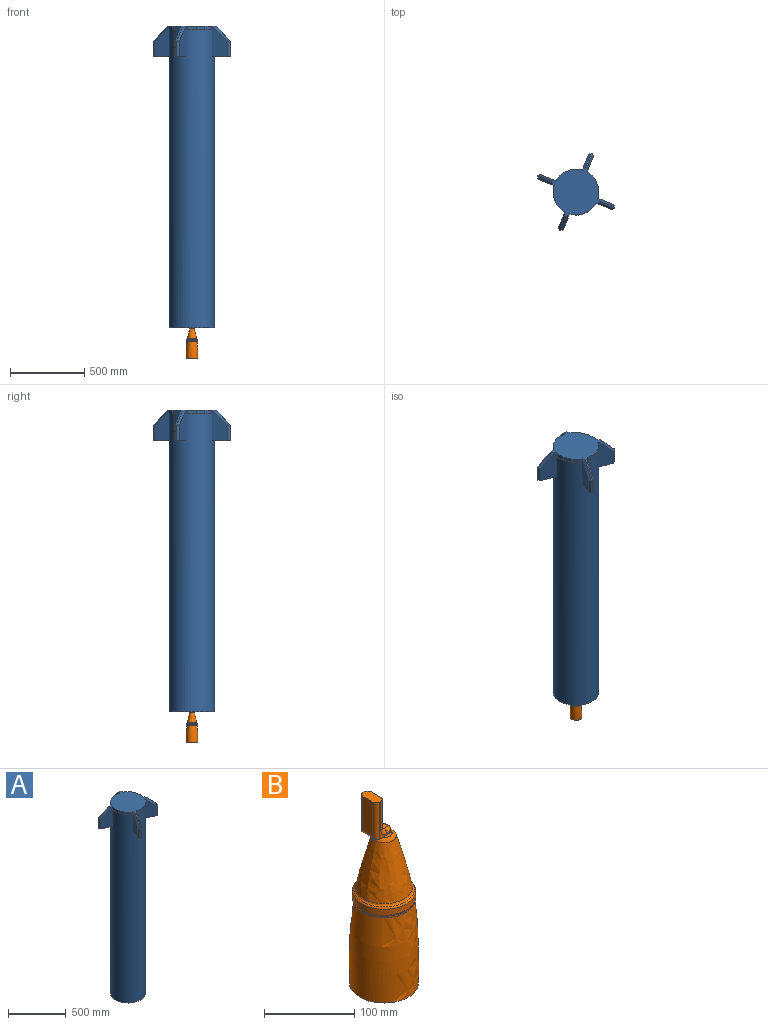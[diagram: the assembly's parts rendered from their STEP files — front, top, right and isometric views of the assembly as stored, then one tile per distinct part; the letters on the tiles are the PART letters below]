
ASSEMBLY  parts=2 mates=2
PART A: 80 faces, bbox 520x520x2032 mm
  f0: plane 203.2x106.54mm, normal (-0.92,0.38,0), area 17697.8mm2, adj f2,f3,f6,f7,f10,f11,f12
  f1: plane 203.2x106.54mm, normal (0.92,-0.38,0), area 17697.8mm2, adj f2,f3,f8,f9,f11,f52,f73
  f2: plane 126.9x76.68mm, normal (0,0,-1), area 4324.7mm2, adj f0,f1,f4,f7,f9,f11
  f3: plane 332.29x332.29mm, normal (0,0,1), area 76585.1mm2, adj f0,f1,f5,f6,f8,f12,f13,f14
  f4: plane 101.6x9.08mm, normal (-0.38,-0.92,0), area 998.6mm2, adj f2,f5,f7,f9
  f5: plane 101.6x97.63mm, normal (-0.27,-0.65,0.71), area 1412.2mm2, adj f3,f4,f6,f8
  f6: plane 115.32x106.86mm, normal (-0.84,-0.19,0.5), area 2647.4mm2, adj f0,f3,f5,f7
  f7: plane 101.6x16.59mm, normal (-0.92,-0.38,0), area 1777.5mm2, adj f0,f2,f4,f6
  f8: plane 106.86x105.6mm, normal (0.46,-0.73,0.5), area 2647.4mm2, adj f1,f3,f5,f9
  f9: plane 101.6x16.59mm, normal (0.38,-0.92,0), area 1777.5mm2, adj f1,f2,f4,f8
  f10: plane 33.56x26.3mm, normal (0,0,-1), area 53.5mm2, adj f0,f11,f12,f51
  f11: cylinder r=152.4mm len=2006.6mm, axis (0,0,-1), area 1896324.1mm2, adj f0,f1,f2,f10,f13,f14,f15,f22
  f12: plane 25.4x11.73mm, normal (-0.38,-0.92,0), area 322.6mm2, adj f0,f3,f10,f51
  f13: plane 203.2x106.54mm, normal (-0.38,-0.92,0), area 17697.8mm2, adj f3,f11,f15,f18,f19,f22,f23
  f14: plane 203.2x106.54mm, normal (0.38,0.92,0), area 17697.8mm2, adj f3,f11,f15,f20,f21,f56,f76
  f15: plane 126.9x76.68mm, normal (0,0,-1), area 4324.7mm2, adj f11,f13,f14,f16,f19,f21
  f16: plane 101.6x9.08mm, normal (0.92,-0.38,0), area 998.6mm2, adj f15,f17,f19,f21
  f17: plane 101.6x97.63mm, normal (0.65,-0.27,0.71), area 1412.2mm2, adj f3,f16,f18,f20
  f18: plane 115.32x106.86mm, normal (0.19,-0.84,0.5), area 2647.4mm2, adj f3,f13,f17,f19
  f19: plane 101.6x16.59mm, normal (0.38,-0.92,0), area 1777.5mm2, adj f13,f15,f16,f18
  f20: plane 106.86x105.6mm, normal (0.73,0.46,0.5), area 2647.4mm2, adj f3,f14,f17,f21
  f21: plane 101.6x16.59mm, normal (0.92,0.38,0), area 1777.5mm2, adj f14,f15,f16,f20
  f22: plane 33.56x26.3mm, normal (0,0,-1), area 53.5mm2, adj f11,f13,f23,f55
  f23: plane 25.4x11.73mm, normal (0.92,-0.38,0), area 322.6mm2, adj f3,f13,f22,f55
  f24: plane 203.2x106.54mm, normal (0.92,-0.38,0), area 17697.8mm2, adj f3,f11,f26,f29,f30,f33,f34
  f25: plane 203.2x106.54mm, normal (-0.92,0.38,0), area 17697.8mm2, adj f3,f11,f26,f31,f32,f60,f67
  f26: plane 126.9x76.68mm, normal (0,0,-1), area 4324.7mm2, adj f11,f24,f25,f27,f30,f32
  f27: plane 101.6x9.08mm, normal (0.38,0.92,0), area 998.6mm2, adj f26,f28,f30,f32
  f28: plane 101.6x97.63mm, normal (0.27,0.65,0.71), area 1412.2mm2, adj f3,f27,f29,f31
  f29: plane 115.32x106.86mm, normal (0.84,0.19,0.5), area 2647.4mm2, adj f3,f24,f28,f30
  f30: plane 101.6x16.59mm, normal (0.92,0.38,0), area 1777.5mm2, adj f24,f26,f27,f29
  f31: plane 106.86x105.6mm, normal (-0.46,0.73,0.5), area 2647.4mm2, adj f3,f25,f28,f32
  f32: plane 101.6x16.59mm, normal (-0.38,0.92,0), area 1777.5mm2, adj f25,f26,f27,f31
  f33: plane 33.56x26.3mm, normal (0,0,-1), area 53.5mm2, adj f11,f24,f34,f59
  f34: plane 25.4x11.73mm, normal (0.38,0.92,0), area 322.6mm2, adj f3,f24,f33,f59
  f35: plane 203.2x106.54mm, normal (0.38,0.92,0), area 17697.8mm2, adj f3,f11,f37,f40,f41,f44,f45
  f36: plane 203.2x106.54mm, normal (-0.38,-0.92,0), area 17697.8mm2, adj f3,f11,f37,f42,f43,f64,f70
  f37: plane 126.9x76.68mm, normal (0,0,-1), area 4324.7mm2, adj f11,f35,f36,f38,f41,f43
  f38: plane 101.6x9.08mm, normal (-0.92,0.38,0), area 998.6mm2, adj f37,f39,f41,f43
  f39: plane 101.6x97.63mm, normal (-0.65,0.27,0.71), area 1412.2mm2, adj f3,f38,f40,f42
  f40: plane 115.32x106.86mm, normal (-0.19,0.84,0.5), area 2647.4mm2, adj f3,f35,f39,f41
  f41: plane 101.6x16.59mm, normal (-0.38,0.92,0), area 1777.5mm2, adj f35,f37,f38,f40
  f42: plane 106.86x105.6mm, normal (-0.73,-0.46,0.5), area 2647.4mm2, adj f3,f36,f39,f43
  f43: plane 101.6x16.59mm, normal (-0.92,-0.38,0), area 1777.5mm2, adj f36,f37,f38,f42
  f44: plane 33.56x26.3mm, normal (0,0,-1), area 53.5mm2, adj f11,f35,f45,f63
  f45: plane 25.4x11.73mm, normal (-0.92,0.38,0), area 322.6mm2, adj f3,f35,f44,f63
  f46: plane 304.8x304.8mm, normal (0,0,-1), area 22295.1mm2, adj f11,f47
  f47: cylinder r=127mm len=254mm, axis (0,0,-1), area 20268.3mm2, adj f46,f48
  f48: plane 254x254mm, normal (0,0,-1), area 50670.7mm2, adj f47
  f49: plane 60.63x25.4mm, normal (-1,0,0), area 1540mm2, adj f3,f50,f64,f70,f71
  f50: plane 56.01x25.4mm, normal (-0.92,-0.38,0), area 1540mm2, adj f3,f49,f51,f71,f72
  f51: plane 42.87x42.87mm, normal (-0.71,-0.71,0), area 1540mm2, adj f3,f10,f12,f50,f72
  f52: plane 25.4x11.73mm, normal (-0.38,-0.92,0), area 322.6mm2, adj f1,f3,f53,f73
  f53: plane 60.63x25.4mm, normal (0,-1,0), area 1540mm2, adj f3,f52,f54,f73,f74
  f54: plane 56.01x25.4mm, normal (0.38,-0.92,0), area 1540mm2, adj f3,f53,f55,f74,f75
  f55: plane 42.87x42.87mm, normal (0.71,-0.71,0), area 1540mm2, adj f3,f22,f23,f54,f75
  f56: plane 25.4x11.73mm, normal (0.92,-0.38,0), area 322.6mm2, adj f3,f14,f57,f76
  f57: plane 60.63x25.4mm, normal (1,0,0), area 1540mm2, adj f3,f56,f58,f65,f76
  f58: plane 56.01x25.4mm, normal (0.92,0.38,0), area 1540mm2, adj f3,f57,f59,f65,f66
  f59: plane 42.87x42.87mm, normal (0.71,0.71,0), area 1540mm2, adj f3,f33,f34,f58,f66
  f60: plane 25.4x11.73mm, normal (0.38,0.92,0), area 322.6mm2, adj f3,f25,f61,f67
  f61: plane 60.63x25.4mm, normal (0,1,0), area 1540mm2, adj f3,f60,f62,f67,f68
  f62: plane 56.01x25.4mm, normal (-0.38,0.92,0), area 1540mm2, adj f3,f61,f63,f68,f69
  f63: plane 42.87x42.87mm, normal (-0.71,0.71,0), area 1540mm2, adj f3,f44,f45,f62,f69
  f64: plane 25.4x11.73mm, normal (-0.92,0.38,0), area 322.6mm2, adj f3,f36,f49,f70
  f65: plane 58.32x11.6mm, normal (0,0,-1), area 59.5mm2, adj f11,f57,f58
  f66: plane 49.44x33.04mm, normal (0,0,-1), area 59.5mm2, adj f11,f58,f59
  f67: plane 42.05x5.8mm, normal (0,0,-1), area 53.5mm2, adj f11,f25,f60,f61
  f68: plane 58.32x11.6mm, normal (0,0,-1), area 59.5mm2, adj f11,f61,f62
  f69: plane 49.44x33.04mm, normal (0,0,-1), area 59.5mm2, adj f11,f62,f63
  f70: plane 42.05x5.8mm, normal (0,0,-1), area 53.5mm2, adj f11,f36,f49,f64
  f71: plane 58.32x11.6mm, normal (0,0,-1), area 59.5mm2, adj f11,f49,f50
  f72: plane 49.44x33.04mm, normal (0,0,-1), area 59.5mm2, adj f11,f50,f51
  f73: plane 42.05x5.8mm, normal (0,0,-1), area 53.5mm2, adj f1,f11,f52,f53
  f74: plane 58.32x11.6mm, normal (0,0,-1), area 59.5mm2, adj f11,f53,f54
  f75: plane 49.44x33.04mm, normal (0,0,-1), area 59.5mm2, adj f11,f54,f55
  f76: plane 42.05x5.8mm, normal (0,0,-1), area 53.5mm2, adj f11,f14,f56,f57
  f77: plane 254x254mm, normal (0,0,-1), area 50670.7mm2, adj f78
  f78: cylinder r=127mm len=1978.66mm, axis (0,0,-1), area 1578900.5mm2, adj f77,f79
  f79: plane 254x254mm, normal (0,0,1), area 50670.7mm2, adj f78
PART B: 36 faces, bbox 103.7x103.7x281.5 mm
  f0: plane 17.77x16.18mm, normal (0,0,1), area 60mm2, adj f2,f13,f18,f20,f21,f24,f27
  f1: bspline ~69.98x62.57mm, area 10492.7mm2, adj f2,f10
  f2: bspline ~27.55x27.54mm, area 482.5mm2, adj f0,f1,f12
  f3: cylinder r=34.92mm len=69.85mm, axis (0,0,1), area 1753.4mm2, adj f8,f9
  f4: bspline ~180.02x78.33mm, area 26438.3mm2, adj f5,f11
  f5: plane 76.23x76.23mm, normal (0,0,-1), area 2533.5mm2, adj f4,f6
  f6: offset ~205.42x103.73mm, area 17662.4mm2, adj f5,f7
  f7: plane 41.78x41.77mm, normal (0,0,-1), area 1370mm2, adj f6
  f8: torus R=32.38mm, axis (0,0,1), area 624.7mm2, adj f3,f10
  f9: bspline ~69.81x69.81mm, area 318.9mm2, adj f3,f11
  f10: bspline ~66.93x66.92mm, area 738.5mm2, adj f1,f8
  f11: bspline ~69.07x69.04mm, area 574.4mm2, adj f4,f9
  f12: plane 25.41x9.94mm, normal (0,0,-1), area 155.9mm2, adj f2,f13,f14,f15,f21,f28,f30
  f13: plane 50.8x15.24mm, normal (0,-1,0), area 167.3mm2, adj f0,f12,f17,f22,f24,f25,f26,f29
  f14: plane 50.8x15.24mm, normal (1,0,0), area 629mm2, adj f12,f17,f21,f22,f23,f28
  f15: plane 50.8x2.54mm, normal (0,1,0), area 129mm2, adj f12,f17,f28,f31
  f16: plane 45.72x15.24mm, normal (-1,0,0), area 696.8mm2, adj f17,f29,f30,f31
  f17: plane 25.4x12.7mm, normal (0,0,1), area 300.4mm2, adj f13,f14,f15,f16,f22,f28,f29,f31
  f18: plane 6.35x2.54mm, normal (0,1,0), area 16.1mm2, adj f0,f19,f21,f27
  f19: plane 7.62x7.62mm, normal (0,0,1), area 52.5mm2, adj f18,f20,f23,f26,f27
  f20: plane 6.35x2.54mm, normal (1,0,0), area 16.1mm2, adj f0,f19,f24,f27
  f21: cylinder r=5.08mm len=11.43mm, axis (0,0,-1), area 70.9mm2, adj f0,f12,f14,f18,f23
  f22: cylinder r=5.08mm len=39.37mm, axis (0,0,1), area 314.2mm2, adj f13,f14,f17,f25
  f23: cylinder r=5.08mm len=12.7mm, axis (0,1,0), area 81.1mm2, adj f14,f19,f21,f25
  f24: cylinder r=5.08mm len=6.35mm, axis (0,0,-1), area 35.9mm2, adj f0,f13,f20,f26
  f25: torus R=10.16mm, axis (0,-1,0), area 86.8mm2, adj f13,f22,f23,f26
  f26: cylinder r=5.08mm len=7.62mm, axis (-1,0,0), area 40.5mm2, adj f13,f19,f24,f25
  f27: cylinder r=5.08mm len=6.35mm, axis (0,0,-1), area 50.7mm2, adj f0,f18,f19,f20
  f28: cylinder r=5.08mm len=50.8mm, axis (0,0,-1), area 405.4mm2, adj f12,f14,f15,f17
  f29: cylinder r=5.08mm len=50.8mm, axis (0,0,-1), area 385.1mm2, adj f13,f16,f17,f30
  f30: cylinder r=5.08mm len=25.4mm, axis (0,-1,0), area 162.1mm2, adj f12,f16,f29,f31
  f31: cylinder r=5.08mm len=50.8mm, axis (0,0,1), area 385.1mm2, adj f15,f16,f17,f30
  f32: plane 6.35x6.35mm, normal (0,0,-1), area 31.7mm2, adj f35
  f33: plane 37.72x37.72mm, normal (0,0,1), area 1116.9mm2, adj f34
  f34: offset ~185.89x103.73mm, area 4743.4mm2, adj f33,f35
  f35: cylinder r=3.17mm len=12.79mm, axis (0,0,1), area 255.1mm2, adj f32,f34
PLACE A t=(345.08,-273.69,-772.6)mm
PLACE B t=(345.08,-273.69,-975.8)mm
MATE planar A.f11 <-> B.f32  axis (0,0,-1) through (345.08,-273.69,-772.6)mm
MATE slider B.f3 <-> A.f11  axis (0,0,-1) through (345.08,-273.69,-975.8)mm
